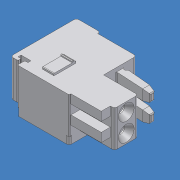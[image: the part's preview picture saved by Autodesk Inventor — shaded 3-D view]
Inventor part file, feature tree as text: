
AUTODESK INVENTOR PART (.ipt)
format: ipt  version: 2012 (Build 160160000, 160)  size: 333,824 bytes
history: native  units: mm (DEFAULTED — no unit token found)
features: sketch x20, extrude x19, pattern_linear x6, revolve x1
ambient origin geometry x8: Origin, YZ Plane, XZ Plane, XY Plane, X Axis, Y Axis, Z Axis, Center Point
bodies: Solid1 (feature_tree)
feature tree (46):
  extrude  "Extrusion1"  Depth=1.5mm TaperAngle=0.0deg
  extrude  "Extrusion2"  Depth=1.5mm TaperAngle=0.0deg
  extrude  "Extrusion3"  Depth=1.5mm TaperAngle=0.0deg
  extrude  "Extrusion4"  Depth=1.5mm TaperAngle=0.0deg
  extrude  "Extrusion5"  TaperAngle=360.0deg  [1 undecoded]
  extrude  "Extrusion6"  Depth=3.3mm TaperAngle=0.0deg
  extrude  "Extrusion7"  Depth=1.0mm TaperAngle=0.0deg
  extrude  "Extrusion8"  Depth=1.0mm TaperAngle=0.0deg
  extrude  "Extrusion9"  Depth=0.9mm TaperAngle=0.0deg
  revolve  "Revolution1"  [1 undecoded]
  pattern_linear  "Rectangular Pattern1"  Count1=2 Spacing1=3.5mm
  extrude  "Extrusion10"  Depth=20.0mm TaperAngle=0.0deg
  pattern_linear  "Rectangular Pattern2"  [2 undecoded]
  extrude  "Extrusion11"  [1 undecoded]
  pattern_linear  "Rectangular Pattern3"  [2 undecoded]
  extrude  "Extrusion12"  [1 undecoded]
  pattern_linear  "Rectangular Pattern4"  [2 undecoded]
  extrude  "Extrusion13"  [1 undecoded]
  extrude  "Extrusion14"  [1 undecoded]
  extrude  "Extrusion15"  [1 undecoded]
  extrude  "Extrusion16"  [1 undecoded]
  extrude  "Extrusion17"  [1 undecoded]
  pattern_linear  "Rectangular Pattern5"  [2 undecoded]
  extrude  "Extrusion18"  [1 undecoded]
  pattern_linear  "Rectangular Pattern6"  [2 undecoded]
  extrude  "Extrusion19"  [1 undecoded]
  sketch  "Skizze_1"  dims[d0=7.0mm d1=0.0mm d2=1.5mm d3=0.0mm]
  sketch  "Skizze_3"  dims[d8=1.5mm d9=0.0mm d10=1.5mm d11=0.0mm]
  sketch  "Skizze_4"  dims[d12=1.5mm d13=0.0mm d14=1.5mm d15=0.0mm]
  sketch  "Skizze_5"  dims[d16=1.4mm d17=0.0mm d18=360.0deg]
  sketch  "Skizze_6"  dims[d19=20.0mm d21=3.5mm d22=10.0mm d24=0.0mm d25=3.3mm d26=0.0mm]
  sketch  "Skizze_7"  dims[d27=20.0mm d29=3.5mm d30=10.0mm d32=0.0mm d33=1.0mm d34=0.0mm]
  sketch  "Skizze_8"  dims[d35=20.0mm d37=3.5mm d38=10.0mm d40=0.0mm d41=1.0mm d42=0.0mm]
  sketch  "Skizze_9"  dims[d43=20.0mm d45=3.5mm d46=10.0mm d48=0.0mm d49=0.9mm d50=0.0mm]
  sketch  "Skizze_2"  dims[d4=1.5mm d5=0.0mm d6=1.5mm d7=0.0mm]
  sketch  "Skizze_10"  dims[d51=0.9mm d52=0.0mm d53=1.7mm d54=0.0mm]
  sketch  "Skizze_12"  dims[d55=1.7mm d56=0.0mm]
  sketch  "Skizze_14"  dims[d57=2.0mm d58=0.0mm d59=20.0mm d61=3.5mm d62=10.0mm d64=0.0mm]
  sketch  "Skizze_16"  dims[d65=1.7mm d66=0.0mm d67=20.0mm d69=3.5mm d70=10.0mm d72=0.0mm]
  sketch  "Skizze_18"  dims[d73=2.2mm d74=0.0mm]
  sketch  "Skizze_19"
  sketch  "Skizze_20"
  sketch  "Skizze_21"
  sketch  "Skizze_22"
  sketch  "Skizze_24"
  sketch  "Skizze_26"
note: 21 required parameter values undecoded (feature->parameter linkage not recoverable at this tier; creation-order binding heuristic only, values carry confidence <= 0.55)